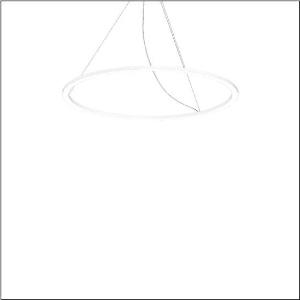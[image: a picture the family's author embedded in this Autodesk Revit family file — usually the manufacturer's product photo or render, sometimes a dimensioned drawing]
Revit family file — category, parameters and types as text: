
# Revit family: silica_r__21_ring-d_5pjbd3d3004a_4211
name_source: partatom
category: Lighting Fixtures
units: mm (PartAtom-declared; Revit-internal decimal feet)

## family parameters
Cut with Voids When Loaded = No
Host = Face
Light Source = No
Part Type = Normal
Room Calculation Point = No
Round Connector Dimension = Use Diameter
Shared = No

## types (1)
- Silica® 21 Ring-D (1 x LED, 8420 lm, 94 W, 4000K)
    Apparent Load = 94 VA
    CIE Flux Codes = 37 69 92 100 100
    Color Rendering = 80
    Color Temperature = 4000K
    Default Elevation = 1800 mm
    Description = Silica® 21 Ring-D, suspended luminaire, of PMMA, frosted, light emission: ring underside luminous distribution, primary light characteristic: symmetric, installation type: suspended mounting, LED, rated luminous flux: 8.420lm, luminous efficacy: 90lm/W, light colour: 840, colour temperature: 4000K, with terminal, 5-pole, mains connection: 230V, AC/DC, 0/50..60Hz, rated input power: 94W, housing, of extruded aluminium section, traffic white (RAL 9016), diameter: 1.100mm, ceiling canopy, traffic white (RAL 9016), protection rating (lamp compartment): IP40, insulation class (complete): insulation class I (protective earthing), certification: CE, impact resistance: IK02, permissible operating ambient temperature: 0..+35°C, packaging unit: 1 piece
    Height = 25 mm  [stored 0.082021 ft]
    Lamp = 1 x LED
    Lamp Light Flux = 8420 lm
    Lamp Power = 94 W
    Lamp count = 1
    Length = 1100 mm
    Luminous efficacy = 90 lm/W
    Manufacturer = Siteco
    ModVariant = No
    Model = 5PJBD3D3004A
    Mounting Place = Ceiling
    Mounting Type = Pendant
    Number of Poles = 1
    OnlyDefault = Yes
    Power Factor = 1
    Product Name = Silica® 21 Ring-D
    Product group = suspended luminaire
    ProductGroupID = 904
    Protection Class = Protection class I
    Protection Degree = Degree of protection
    RLX_Detail_Level = 1
    RLX_Emergency_Light_Flux = 0 lm
    RLX_Emergency_Type = 0
    RLX_Emergency_Type_DB = No
    RlxData = <blob elided: 12481 chars, md5=3dd2df42>
    Socket = socket
    Standby Power = 0 W
    System Light Flux = 8420 lm
    System Power = 94 W
    Type Comments = Product without accessories
    Type Image = l_1258355.jpg
    URL = http://relux.com
    VarID = ---
    Voltage = 0 V
    Weight = 0.00 kg
    Width = 0 mm  [stored 0 ft]

note: [stored X ft] marks values corroborated as IEEE doubles in the binary element streams (Revit-internal decimal feet)

## geometry (parser evidence)
native form markers: Sweep x8
no freeform markers — native parametric forms only
